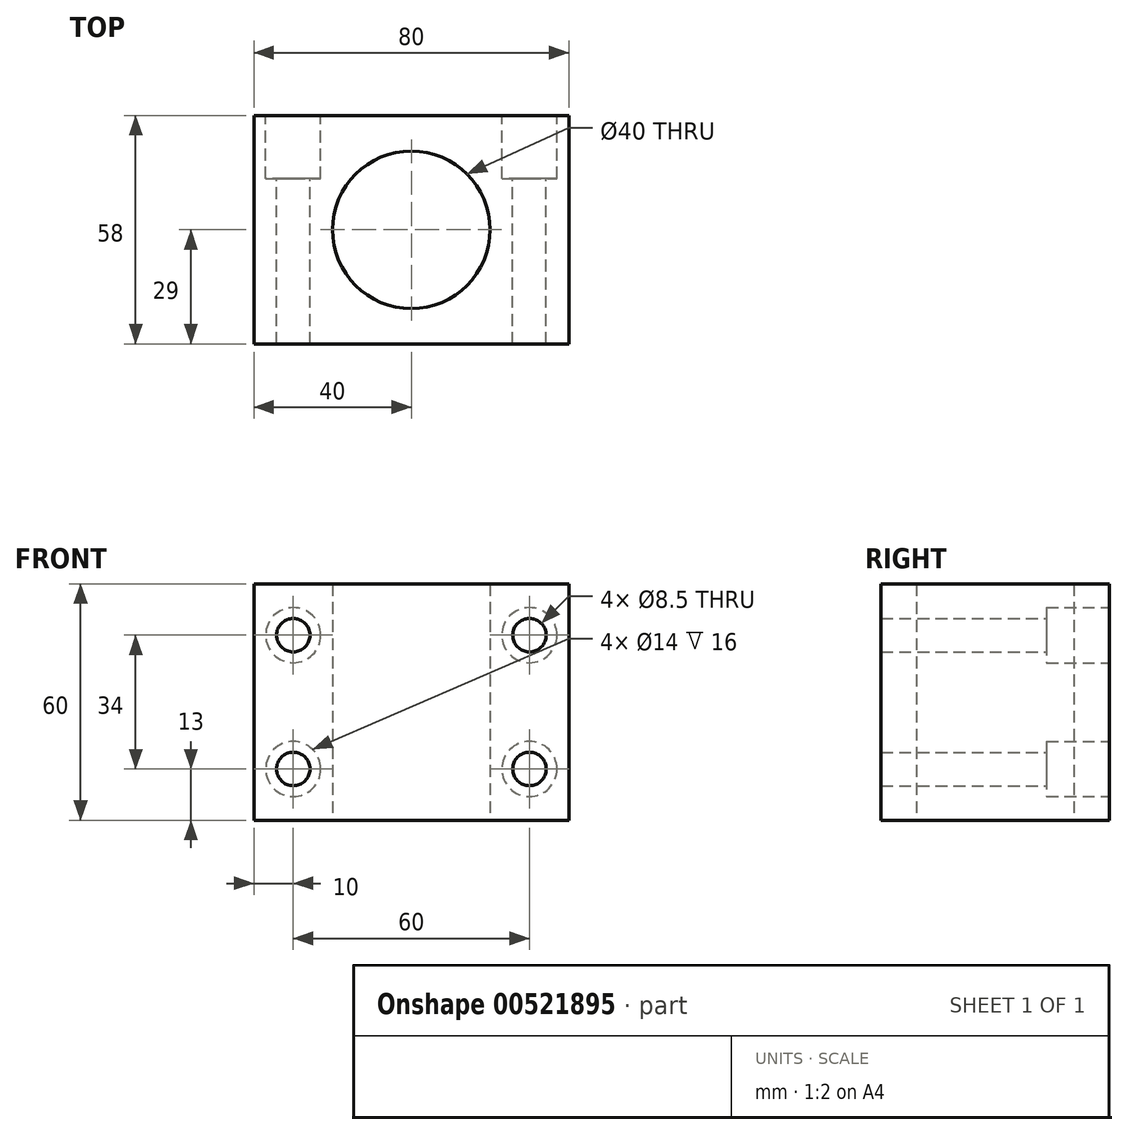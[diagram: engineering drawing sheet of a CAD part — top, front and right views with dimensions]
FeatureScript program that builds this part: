
annotation { "Feature Type Name" : "Feature", "Feature Type Description" : "" }
export const myFeature = defineFeature(function(context is Context, id is Id, definition is map)
    precondition{}
    {
        {
            var Q0;
            Q0=qCreatedBy(makeId("Top.planeOp"),FACE);
            var sketch = newSketch(context, id + "F0", { "sketchPlane" : qUnion([Q0])});
            skCircle(sketch, "E0", {"center": v(0, 0) * mm, "radius": 20 * mm});
            skLineSegment(sketch, "E1.bottom", {"start": v(-40, 29) * mm, "end": v(40, 29) * mm});
            skLineSegment(sketch, "E1.top", {"start": v(-40, -29) * mm, "end": v(40, -29) * mm});
            skLineSegment(sketch, "E1.left", {"start": v(-40, 29) * mm, "end": v(-40, -29) * mm});
            skLineSegment(sketch, "E1.right", {"start": v(40, 29) * mm, "end": v(40, -29) * mm});
            skSolve(sketch);
        }
        {
            var Q0;
            Q0 = qSketchRegion(id + "F0", true);
            extrude(context, id + "F1", {"entities" : qUnion([Q0]), "depth" : 60 * mm, "offsetDistance" : 25 * mm});
        }
        {
            var Q0;
            Q0=makeQuery(id+"F1.opExtrude","SWEPT_FACE",FACE,{"disambiguationData":[OSD([sQuery(id+"F0.wireOp",EDGE,"E1.bottom")])]});
            var sketch = newSketch(context, id + "F2", { "sketchPlane" : qUnion([Q0])});
            skCircle(sketch, "E2", {"center": v(30, 47) * mm, "radius": 7 * mm});
            skCircle(sketch, "E3", {"center": v(-30, 47) * mm, "radius": 7 * mm});
            skCircle(sketch, "E4", {"center": v(30, 13) * mm, "radius": 7 * mm});
            skCircle(sketch, "E5", {"center": v(-30, 13) * mm, "radius": 7 * mm});
            skLineSegment(sketch, "E6", {"start": v(40, 30) * mm, "end": v(-40, 30) * mm, "construction": true});
            skCircle(sketch, "E7", {"center": v(30, 13) * mm, "radius": 4.25 * mm});
            skCircle(sketch, "E8", {"center": v(30, 47) * mm, "radius": 4.25 * mm});
            skCircle(sketch, "E9", {"center": v(-30, 13) * mm, "radius": 4.25 * mm});
            skCircle(sketch, "E10", {"center": v(-30, 47) * mm, "radius": 4.25 * mm});
            skSolve(sketch);
        }
        {
            var Q0;
            Q0=makeQuery(id+"F2.imprint","IMPRINT",FACE,{"disambiguationData":[TD([[makeQuery(id+"F2.imprint","IMPRINT",EDGE,{"derivedFrom":sQuery(id+"F2.wireOp",EDGE,"E7")}),1.0]])]});
            var Q1;
            Q1=makeQuery(id+"F2.imprint","IMPRINT",FACE,{"disambiguationData":[TD([[makeQuery(id+"F2.imprint","IMPRINT",EDGE,{"derivedFrom":sQuery(id+"F2.wireOp",EDGE,"E9")}),1.0]])]});
            var Q2;
            Q2=makeQuery(id+"F2.imprint","IMPRINT",FACE,{"disambiguationData":[TD([[makeQuery(id+"F2.imprint","IMPRINT",EDGE,{"derivedFrom":sQuery(id+"F2.wireOp",EDGE,"E10")}),1.0]])]});
            var Q3;
            Q3=makeQuery(id+"F2.imprint","IMPRINT",FACE,{"disambiguationData":[TD([[makeQuery(id+"F2.imprint","IMPRINT",EDGE,{"derivedFrom":sQuery(id+"F2.wireOp",EDGE,"E8")}),1.0]])]});
            extrude(context, id + "F3", {"entities" : qUnion([Q0, Q1, Q2, Q3]), "operationType" : NewBodyOperationType.REMOVE, "endBound" : BoundingType.THROUGH_ALL, "oppositeDirection" : true, "depth" : 25 * mm, "offsetDistance" : 25 * mm});
        }
        {
            var Q0;
            Q0=makeQuery(id+"F2.imprint","IMPRINT",FACE,{"disambiguationData":[TD([[makeQuery(id+"F2.imprint","IMPRINT",EDGE,{"derivedFrom":sQuery(id+"F2.wireOp",EDGE,"E4")}),1.0]])]});
            var Q1;
            Q1=makeQuery(id+"F2.imprint","IMPRINT",FACE,{"disambiguationData":[TD([[makeQuery(id+"F2.imprint","IMPRINT",EDGE,{"derivedFrom":sQuery(id+"F2.wireOp",EDGE,"E5")}),1.0]])]});
            var Q2;
            Q2=makeQuery(id+"F2.imprint","IMPRINT",FACE,{"disambiguationData":[TD([[makeQuery(id+"F2.imprint","IMPRINT",EDGE,{"derivedFrom":sQuery(id+"F2.wireOp",EDGE,"E3")}),1.0]])]});
            var Q3;
            Q3=makeQuery(id+"F2.imprint","IMPRINT",FACE,{"disambiguationData":[TD([[makeQuery(id+"F2.imprint","IMPRINT",EDGE,{"derivedFrom":sQuery(id+"F2.wireOp",EDGE,"E2")}),1.0]])]});
            extrude(context, id + "F4", {"entities" : qUnion([Q0, Q1, Q2, Q3]), "operationType" : NewBodyOperationType.REMOVE, "oppositeDirection" : true, "depth" : 16 * mm, "offsetDistance" : 25 * mm});
        }
    });
